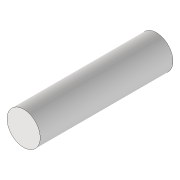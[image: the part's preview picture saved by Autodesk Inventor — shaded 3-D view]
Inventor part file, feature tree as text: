
AUTODESK INVENTOR PART (.ipt)
format: ipt  version: 2020 (Build 240168000, 168)  size: 76,288 bytes
history: native  units: mm
features: extrude x1, sketch x1
ambient origin geometry x8: Origin, YZ Plane, XZ Plane, XY Plane, X Axis, Y Axis, Z Axis, Center Point
bodies: Volumenkörper1 (feature_tree)
feature tree (2):
  extrude  "Extrusion1"  Depth=2.0mm TaperAngle=0.0deg
  sketch  "Skizze1"  dims[d0=0.5mm d1=2.0mm d2=0.0mm]
